AUTODESK INVENTOR PART (.ipt)
format: ipt  version: 2017 (Build 210142000, 142)  size: 118,784 bytes
history: native  units: mm
features: plane x4, other x3, sketch x2, extrude x2, reference x2, chamfer x1
ambient origin geometry x8: Origin, YZ Plane, XZ Plane, XY Plane, X Axis, Y Axis, Z Axis, Center Point
bodies: Body1 (feature_tree)
feature tree (14):
  plane  "Arbeitsebene1"
  sketch  "Skizze1"  dims[d0=0.1mm d1=0.1mm]
  plane  "Arbeitsebene2"
  plane  "Arbeitsebene3"
  plane  "Arbeitsebene4"
  extrude  "Extrusion2"  Depth=0.1mm
  extrude  "Extrusion3"  Depth=4.0mm
  chamfer  "Fase1"  Distance=4.0mm
  reference  "Referenz1"
  sketch  "Skizze2"  dims[d2=0.1mm d3=0.1mm d6=4.0mm d7=4.0mm d8=4.0mm d9=4.0mm d10=10.0mm d11=0.0mm d12=10.0mm d13=0.0mm d14=2.4mm d15=2.0mm d16=45.0deg]
  reference  "Referenz2"
  other  "<userpath>\Dropbox\Elektronik\aXe_Dashboard240XL\Gehäuse\DisplayDummyAuschnitt.iam"
  other  "DisplayDummyAuschnitt.iam"
  other  "DisplayDummy:1"
